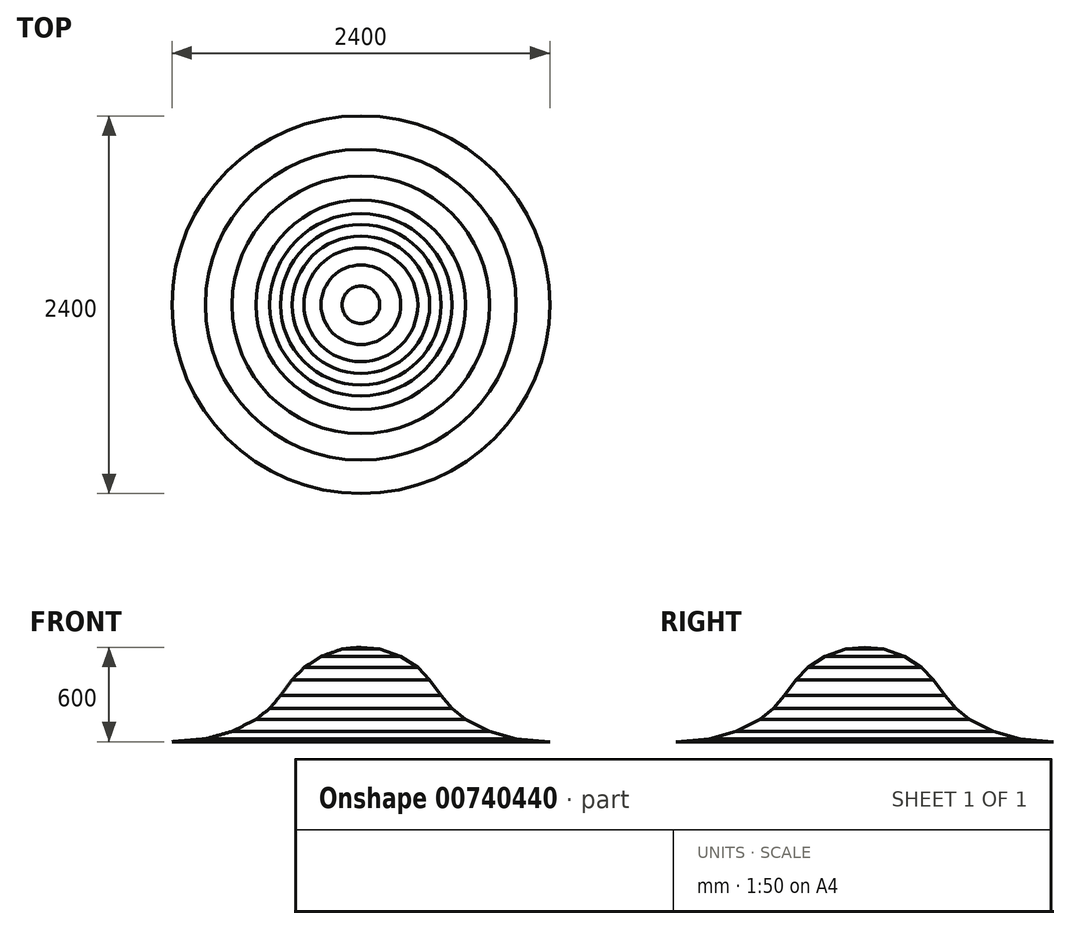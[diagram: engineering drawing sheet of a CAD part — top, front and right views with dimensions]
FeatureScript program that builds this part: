
annotation { "Feature Type Name" : "Feature", "Feature Type Description" : "" }
export const myFeature = defineFeature(function(context is Context, id is Id, definition is map)
    precondition{}
    {
        {
            var Q0;
            Q0=qCreatedBy(makeId("Front.planeOp"),FACE);
            var sketch = newSketch(context, id + "F0", { "sketchPlane" : qUnion([Q0])});
            skLineSegment(sketch, "E0", {"start": v(0, 0) * mm, "end": v(0, 600) * mm});
            skLineSegment(sketch, "E1", {"start": v(0, 600) * mm, "end": v(-119.66, 588.1) * mm});
            skLineSegment(sketch, "E2", {"start": v(-119.66, 588.1) * mm, "end": v(-252.72, 541.54) * mm});
            skLineSegment(sketch, "E3", {"start": v(-252.72, 541.54) * mm, "end": v(-361.39, 470.57) * mm});
            skLineSegment(sketch, "E4", {"start": v(-361.39, 470.57) * mm, "end": v(-436.79, 392.95) * mm});
            skLineSegment(sketch, "E5", {"start": v(-436.79, 392.95) * mm, "end": v(-509.97, 293.15) * mm});
            skLineSegment(sketch, "E6", {"start": v(-509.97, 293.15) * mm, "end": v(-578.72, 211.1) * mm});
            skLineSegment(sketch, "E7", {"start": v(-578.72, 211.1) * mm, "end": v(-665.21, 142.35) * mm});
            skLineSegment(sketch, "E8", {"start": v(-665.21, 142.35) * mm, "end": v(-818.23, 64.73) * mm});
            skLineSegment(sketch, "E9", {"start": v(-818.23, 64.73) * mm, "end": v(-986.78, 18.16) * mm});
            skLineSegment(sketch, "E10", {"start": v(-986.78, 18.16) * mm, "end": v(-1200, 0) * mm});
            skLineSegment(sketch, "E11", {"start": v(-1200, 0) * mm, "end": v(0, 0) * mm});
            skSolve(sketch);
        }
        {
            var Q0;
            Q0 = qSketchRegion(id + "F0", true);
            var Q1;
            Q1=sQuery(id+"F0.wireOp",EDGE,"E0");
            revolve(context, id + "F1", {"surfaceOperationType" : NewSurfaceOperationType.NEW, "entities" : qUnion([Q0]), "axis" : qUnion([Q1]), "revolveType" : RevolveType.FULL});
        }
    });
